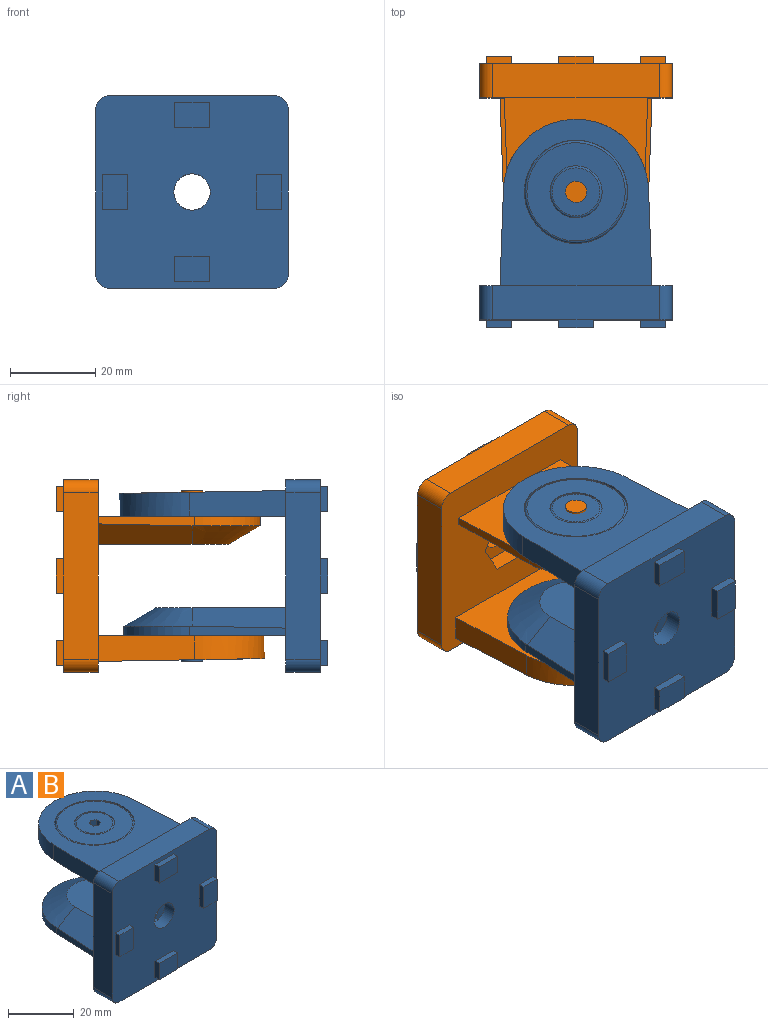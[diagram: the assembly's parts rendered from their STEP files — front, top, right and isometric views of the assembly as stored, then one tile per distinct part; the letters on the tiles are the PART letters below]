
ASSEMBLY  parts=2 mates=1
PART A: 70 faces, bbox 45.1x48.9x45.1 mm
  f0: plane 22.61x6mm, normal (1,0.04,0), area 131.3mm2, adj f12,f13,f17,f69
  f1: plane 30.5x17mm, normal (0,0,1), area 487.5mm2, adj f5,f6,f7,f13
  f2: plane 22.61x6mm, normal (-1,0.04,0), area 131.3mm2, adj f12,f13,f17,f69
  f3: plane 22.58x2.28mm, normal (-1,0.04,0), area 46.1mm2, adj f5,f6,f10,f11,f13
  f4: plane 22.58x2.28mm, normal (1,0.04,0), area 46.1mm2, adj f5,f7,f10,f11,f13
  f5: cone r=18.89mm half-angle=60deg, axis (0,0,-1), area 333.3mm2, adj f1,f3,f4,f6,f7,f11
  f6: plane 22x8.3mm, normal (-0.5,0,0.87), area 200.8mm2, adj f1,f3,f5,f13
  f7: plane 22x8.3mm, normal (0.5,0,0.87), area 200.8mm2, adj f1,f4,f5,f13
  f8: plane 5x5mm, normal (0,0,-1), area 19.6mm2, adj f9
  f9: cylinder r=2.5mm len=6mm, axis (0,0,1), area 94.2mm2, adj f8,f10
  f10: plane 38x33.6mm, normal (0,0,-1), area 1104.3mm2, adj f3,f4,f9,f11,f13
  f11: cylinder r=16mm len=31.98mm, axis (0,0,1), area 111.5mm2, adj f3,f4,f5,f10
  f12: plane 39.09x35.69mm, normal (0,0.02,1), area 760mm2, adj f0,f2,f13,f19,f69
  f13: plane 45x45mm, normal (0,1,0), area 1451.9mm2, adj f0,f1,f2,f3,f4,f6,f7,f10
  f14: plane 39x8mm, normal (-1,0,0), area 312mm2, adj f13,f22,f23,f28
  f15: cylinder r=4.25mm len=8.5mm, axis (0,1,0), area 106.8mm2, adj f28,f68
  f16: plane 39x8mm, normal (1,0,0), area 312mm2, adj f13,f25,f26,f28
  f17: plane 39x35.6mm, normal (0,0,-1), area 1200.2mm2, adj f0,f2,f13,f18,f69
  f18: cylinder r=2.5mm len=5mm, axis (0,0,1), area 15.7mm2, adj f17,f20
  f19: cylinder r=12.1mm len=24.2mm, axis (0,0,1), area 199.4mm2, adj f12,f21
  f20: plane 5x5mm, normal (0,0,-1), area 19.6mm2, adj f18
  f21: plane 24.2x24.2mm, normal (0,0,1), area 7.6mm2, adj f19,f54
  f22: cylinder r=3mm len=8mm, axis (0,1,0), area 37.7mm2, adj f13,f14,f27,f28
  f23: cylinder r=3mm len=8mm, axis (0,1,0), area 37.7mm2, adj f13,f14,f24,f28
  f24: plane 39x8mm, normal (0,0,1), area 312mm2, adj f13,f23,f25,f28
  f25: cylinder r=3mm len=8mm, axis (0,1,0), area 37.7mm2, adj f13,f16,f24,f28
  f26: cylinder r=3mm len=8mm, axis (0,1,0), area 37.7mm2, adj f13,f16,f27,f28
  f27: plane 39x8mm, normal (0,0,-1), area 312mm2, adj f13,f22,f26,f28
  f28: plane 45x45mm, normal (0,-1,0), area 1768.5mm2, adj f14,f15,f16,f22,f23,f24,f25,f26
  f29: plane 8x1.8mm, normal (-1,0,0), area 14.4mm2, adj f28,f30,f32,f33
  f30: plane 8x6mm, normal (0,-1,0), area 48mm2, adj f29,f31,f32,f33
  f31: plane 8x1.8mm, normal (1,0,0), area 14.4mm2, adj f28,f30,f32,f33
  f32: plane 6x1.8mm, normal (0,0,-1), area 10.8mm2, adj f28,f29,f30,f31
  f33: plane 6x1.8mm, normal (0,0,1), area 10.8mm2, adj f28,f29,f30,f31
  f34: plane 8x1.8mm, normal (-1,0,0), area 14.4mm2, adj f28,f35,f37,f38
  f35: plane 8x6mm, normal (0,-1,0), area 48mm2, adj f34,f36,f37,f38
  f36: plane 8x1.8mm, normal (1,0,0), area 14.4mm2, adj f28,f35,f37,f38
  f37: plane 6x1.8mm, normal (0,0,-1), area 10.8mm2, adj f28,f34,f35,f36
  f38: plane 6x1.8mm, normal (0,0,1), area 10.8mm2, adj f28,f34,f35,f36
  f39: plane 8x1.8mm, normal (0,0,1), area 14.4mm2, adj f28,f40,f42,f43
  f40: plane 8x6mm, normal (0,-1,0), area 48mm2, adj f39,f41,f42,f43
  f41: plane 8x1.8mm, normal (0,0,-1), area 14.4mm2, adj f28,f40,f42,f43
  f42: plane 6x1.8mm, normal (-1,0,0), area 10.8mm2, adj f28,f39,f40,f41
  f43: plane 6x1.8mm, normal (1,0,0), area 10.8mm2, adj f28,f39,f40,f41
  f44: plane 8x1.8mm, normal (0,0,1), area 14.4mm2, adj f28,f45,f47,f48
  f45: plane 8x6mm, normal (0,-1,0), area 48mm2, adj f44,f46,f47,f48
  f46: plane 8x1.8mm, normal (0,0,-1), area 14.4mm2, adj f28,f45,f47,f48
  f47: plane 6x1.8mm, normal (-1,0,0), area 10.8mm2, adj f28,f44,f45,f46
  f48: plane 6x1.8mm, normal (1,0,0), area 10.8mm2, adj f28,f44,f45,f46
  f49: plane 11.2x11.2mm, normal (0,0,1), area 90.7mm2, adj f50,f55,f56,f57,f58,f59,f60
  f50: torus R=5.6mm, axis (0,0,-1), area 29.2mm2, adj f49,f51
  f51: cylinder r=6.1mm len=12.2mm, axis (0,0,1), area 19.2mm2, adj f50,f52
  f52: plane 23x23mm, normal (0,0,1), area 298.6mm2, adj f51,f53
  f53: torus R=11.5mm, axis (0,0,-1), area 58.3mm2, adj f52,f54
  f54: cylinder r=12mm len=24mm, axis (0,0,1), area 154.6mm2, adj f21,f53
  f55: plane 3x1.73mm, normal (1,0,0), area 5.2mm2, adj f49,f56,f60,f61
  f56: plane 3x1.5mm, normal (0.5,0.87,0), area 5.2mm2, adj f49,f55,f57,f61
  f57: plane 3x1.5mm, normal (-0.5,0.87,0), area 5.2mm2, adj f49,f56,f58,f61
  f58: plane 3x1.73mm, normal (-1,0,0), area 5.2mm2, adj f49,f57,f59,f61
  f59: plane 3x1.5mm, normal (-0.5,-0.87,0), area 5.2mm2, adj f49,f58,f60,f61
  f60: plane 3x1.5mm, normal (0.5,-0.87,0), area 5.2mm2, adj f49,f55,f59,f61
  f61: plane 3.46x3mm, normal (0,0,1), area 7.8mm2, adj f55,f56,f57,f58,f59,f60
  f62: plane 7x4.04mm, normal (0.87,0,0.5), area 32.3mm2, adj f13,f63,f67,f68
  f63: plane 7x4.04mm, normal (0.87,0,-0.5), area 32.3mm2, adj f13,f62,f64,f68
  f64: plane 8.08x4mm, normal (0,0,-1), area 32.3mm2, adj f13,f63,f65,f68
  f65: plane 7x4.04mm, normal (-0.87,0,-0.5), area 32.3mm2, adj f13,f64,f66,f68
  f66: plane 7x4.04mm, normal (-0.87,0,0.5), area 32.3mm2, adj f13,f65,f67,f68
  f67: plane 8.08x4mm, normal (0,0,1), area 32.3mm2, adj f13,f62,f66,f68
  f68: plane 16.17x14mm, normal (0,1,0), area 113mm2, adj f15,f62,f63,f64,f65,f66,f67
  f69: cylinder r=17mm len=33.98mm, axis (0,0,1), area 283mm2, adj f0,f2,f12,f17
PART B: same geometry as A
PLACE A t=(-2.8,30.3,10.73)mm
PLACE B rot(axis=(1,0,0),180deg) t=(-2.8,30.3,10.73)mm
MATE revolute B.f5 <-> A.f5  axis (0,0,1) through (-2.8,30.3,24.73)mm
